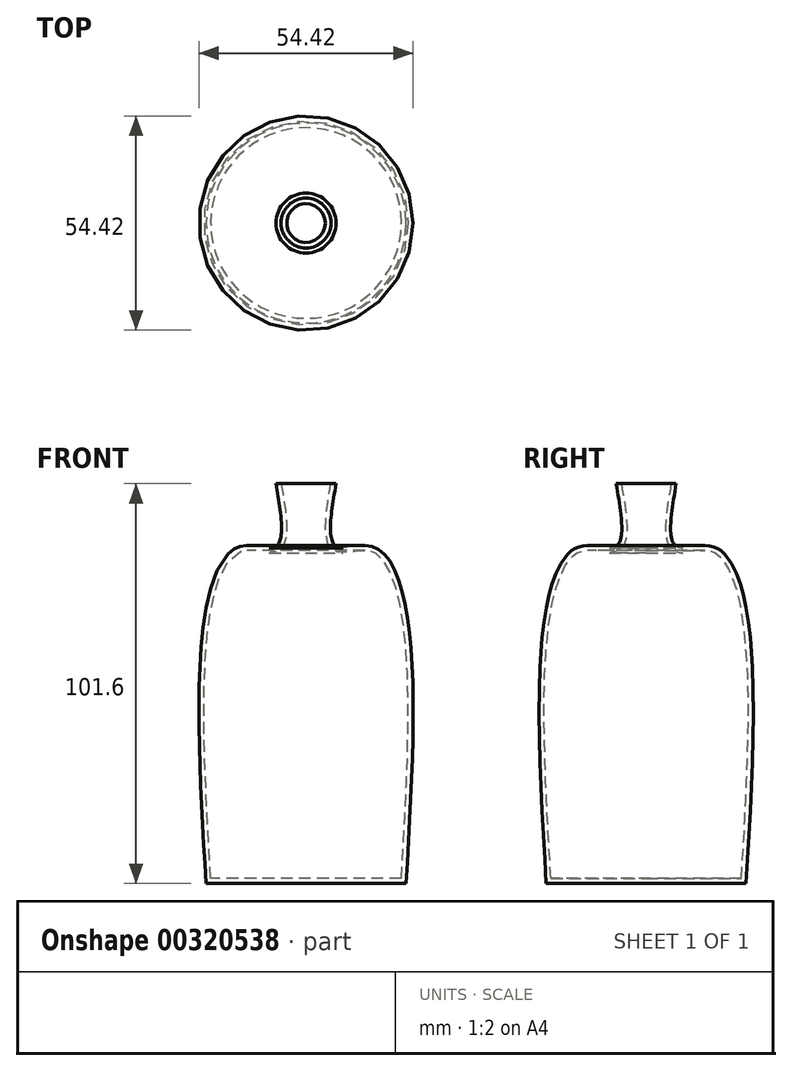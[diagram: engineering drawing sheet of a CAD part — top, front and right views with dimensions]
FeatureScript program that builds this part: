
annotation { "Feature Type Name" : "Feature", "Feature Type Description" : "" }
export const myFeature = defineFeature(function(context is Context, id is Id, definition is map)
    precondition{}
    {
        {
            var Q0;
            Q0=qCreatedBy(makeId("Front.planeOp"),FACE);
            var sketch = newSketch(context, id + "F0", { "sketchPlane" : qUnion([Q0])});
            skLineSegment(sketch, "E0", {"start": v(0, -58.8) * mm, "end": v(0, 42.8) * mm, "construction": true});
            skLineSegment(sketch, "E1", {"start": v(0, -58.8) * mm, "end": v(-25.4, -58.8) * mm});
            skLineSegment(sketch, "E2", {"start": v(0, 42.8) * mm, "end": v(-7.62, 42.8) * mm});
            skLineSegment(sketch, "E3", {"start": v(-7.62, 11.05) * mm, "end": v(-25.4, 11.05) * mm, "construction": true});
            skLineSegment(sketch, "E4", {"start": v(-7.62, 42.8) * mm, "end": v(-7.62, 11.05) * mm, "construction": true});
            skLineSegment(sketch, "E5", {"start": v(-7.62, 26.93) * mm, "end": v(-16.5, 26.93) * mm, "construction": true});
            skLineSegment(sketch, "E6", {"start": v(-16.5, 26.93) * mm, "end": v(-16.5, 11.05) * mm, "construction": true});
            skFitSpline(sketch, "E7", {"points": [v(-25.4, -58.8) * mm, v(-25.4, 11.05) * mm, v(-16.5, 26.93) * mm, v(-7.62, 26.93) * mm, v(-7.62, 42.8) * mm], "startDerivative": vector(-11.02, 185.8) * mm, "endDerivative": vector(-18.2, 105.2) * mm});
            skLineSegment(sketch, "E8", {"start": v(0, 42.8) * mm, "end": v(0, -58.8) * mm});
            skSolve(sketch);
        }
        {
            var Q0;
            Q0=makeQuery(id+"F0.imprint","IMPRINT",FACE,{"disambiguationData":[TD([[makeQuery(id+"F0.imprint","IMPRINT",EDGE,{"derivedFrom":sQuery(id+"F0.wireOp",EDGE,"E1")}),-1.0]])]});
            var Q1;
            Q1=sQuery(id+"F0.wireOp",EDGE,"E8");
            revolve(context, id + "F1", {"entities" : qUnion([Q0]), "axis" : qUnion([Q1]), "revolveType" : RevolveType.FULL});
        }
        {
            var Q0;
            Q0=makeQuery(id+"F1.opRevolve","SWEPT_FACE",FACE,{"disambiguationData":[OSD([sQuery(id+"F0.wireOp",EDGE,"E2")])]});
            shell(context, id + "F2", {"entities" : qUnion([Q0]), "thickness" : 1.27 * mm});
        }
    });
